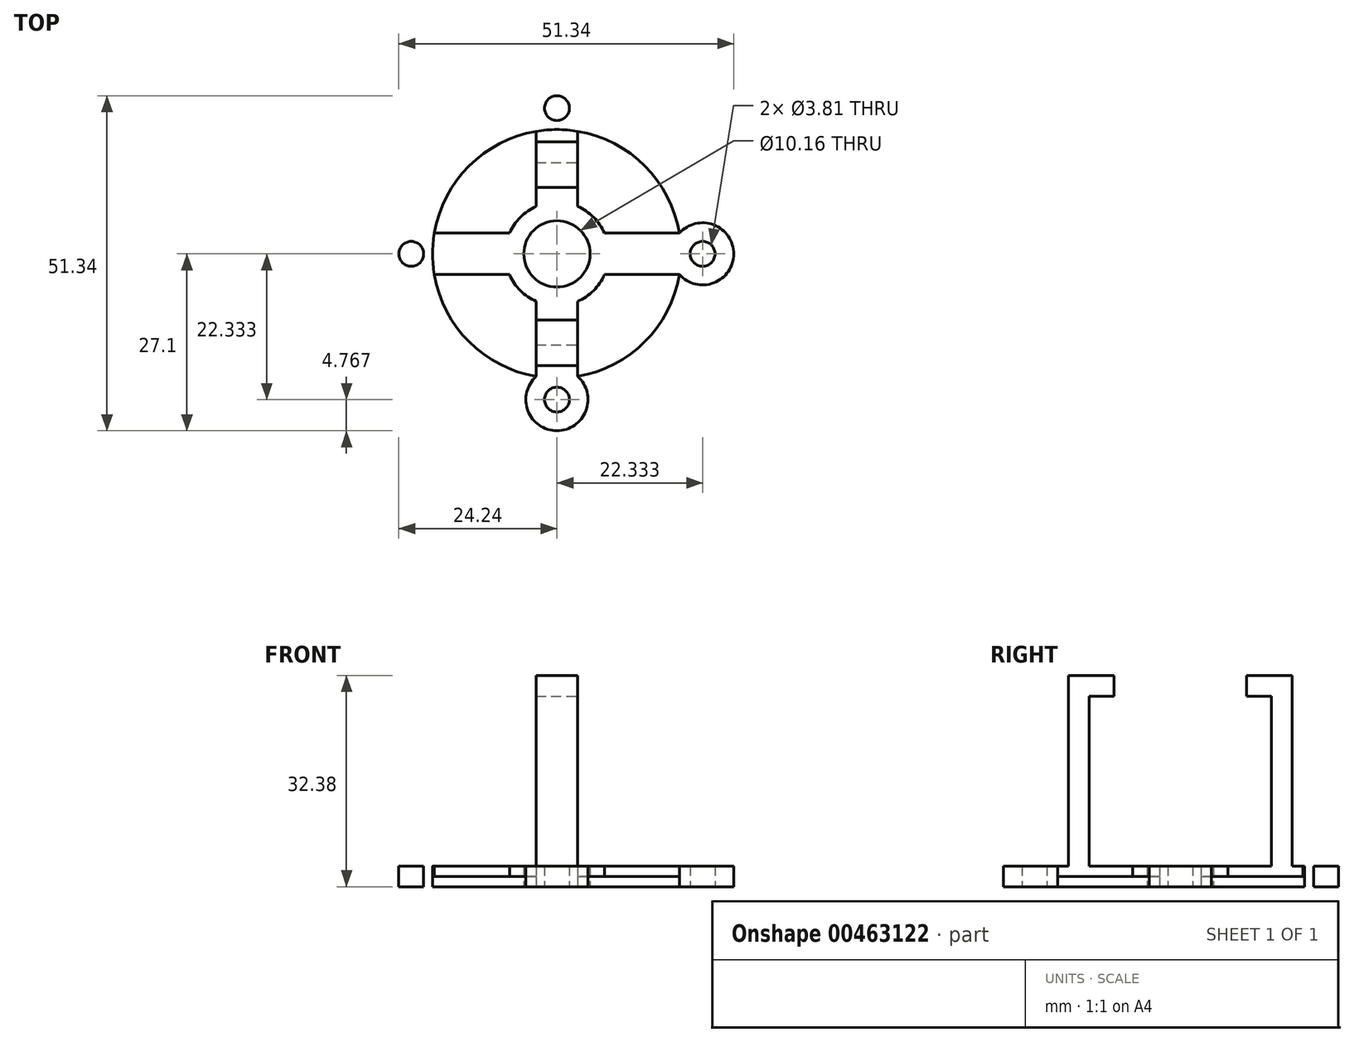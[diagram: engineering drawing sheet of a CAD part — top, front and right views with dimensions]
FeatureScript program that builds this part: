
annotation { "Feature Type Name" : "Feature", "Feature Type Description" : "" }
export const myFeature = defineFeature(function(context is Context, id is Id, definition is map)
    precondition{}
    {
        {
            var Q0;
            Q0=qCreatedBy(makeId("Top.planeOp"),FACE);
            var sketch = newSketch(context, id + "F0", { "sketchPlane" : qUnion([Q0])});
            skCircle(sketch, "E0", {"center": v(0, 0) * mm, "radius": 5.08 * mm});
            skCircle(sketch, "E1", {"center": v(0, 0) * mm, "radius": 19.05 * mm});
            skCircle(sketch, "E2", {"center": v(0, 0) * mm, "radius": 7.94 * mm});
            skLineSegment(sketch, "E3", {"start": v(-3.18, -7.27) * mm, "end": v(-3.18, -18.78) * mm});
            skLineSegment(sketch, "E4", {"start": v(0, 0) * mm, "end": v(3.6, 3.6) * mm});
            skLineSegment(sketch, "E5.MirrorCS", {"start": v(3.18, -7.27) * mm, "end": v(3.18, -18.78) * mm});
            skLineSegment(sketch, "E6.MirrorCS", {"start": v(3.18, 7.27) * mm, "end": v(3.18, 18.78) * mm});
            skLineSegment(sketch, "E7.MirrorCS", {"start": v(-3.18, 7.27) * mm, "end": v(-3.18, 18.78) * mm});
            skLineSegment(sketch, "E8.MirrorCS", {"start": v(-7.27, -3.17) * mm, "end": v(-18.78, -3.17) * mm});
            skLineSegment(sketch, "E9.MirrorCS", {"start": v(-7.27, 3.18) * mm, "end": v(-18.78, 3.18) * mm});
            skLineSegment(sketch, "E10.MirrorCS", {"start": v(7.27, -3.17) * mm, "end": v(18.78, -3.17) * mm});
            skLineSegment(sketch, "E11.MirrorCS", {"start": v(7.27, 3.18) * mm, "end": v(18.78, 3.18) * mm});
            skCircle(sketch, "E12", {"center": v(0, -22.33) * mm, "radius": 4.76 * mm});
            skPoint(sketch, "E12.third.point", {"position": v(3.18, -25.88) * mm});
            skCircle(sketch, "E13.MirrorC", {"center": v(0, 22.33) * mm, "radius": 4.76 * mm});
            skCircle(sketch, "E14.MirrorC", {"center": v(-22.33, 0) * mm, "radius": 4.76 * mm});
            skCircle(sketch, "E15.MirrorC", {"center": v(22.33, 0) * mm, "radius": 4.76 * mm});
            skLineSegment(sketch, "E16.bottom", {"start": v(-3.18, -17.15) * mm, "end": v(3.18, -17.15) * mm});
            skLineSegment(sketch, "E16.top", {"start": v(-3.18, -13.97) * mm, "end": v(3.18, -13.97) * mm});
            skLineSegment(sketch, "E16.left", {"start": v(-3.18, -17.15) * mm, "end": v(-3.18, -13.97) * mm});
            skLineSegment(sketch, "E16.right", {"start": v(3.18, -17.15) * mm, "end": v(3.18, -13.97) * mm});
            skLineSegment(sketch, "E17.MirrorCS", {"start": v(-3.18, 13.97) * mm, "end": v(3.18, 13.97) * mm});
            skLineSegment(sketch, "E18.MirrorCS", {"start": v(-3.18, 17.15) * mm, "end": v(3.18, 17.15) * mm});
            skCircle(sketch, "E19", {"center": v(0, -22.33) * mm, "radius": 1.9 * mm});
            skCircle(sketch, "E20.MirrorC", {"center": v(0, 22.33) * mm, "radius": 1.9 * mm});
            skCircle(sketch, "E21.MirrorC", {"center": v(-22.33, 0) * mm, "radius": 1.9 * mm});
            skCircle(sketch, "E22.MirrorC", {"center": v(22.33, 0) * mm, "radius": 1.9 * mm});
            skSolve(sketch);
        }
        {
            var Q0;
            {var subQ0=sQuery(id+"F0.wireOp",EDGE,"E10.MirrorCS");Q0=makeQuery(id+"F0.imprint","IMPRINT",FACE,{"disambiguationData":[TD([[makeQuery(id+"F0.imprint","IMPRINT",EDGE,{"derivedFrom":subQ0}),1.0]])]});}
            var Q1;
            {var subQ0=sQuery(id+"F0.wireOp",EDGE,"E15.MirrorC");var subQ1=sQuery(id+"F0.wireOp",EDGE,"E1");var subQ2=makeQuery(id+"F0.imprint","INTERSECT",VERTEX,{"derivedFrom":[subQ1,sQuery(id+"F0.wireOp",EDGE,"E10.MirrorCS"),subQ0]});Q1=makeQuery(id+"F0.imprint","IMPRINT",FACE,{"disambiguationData":[TD([[makeQuery(id+"F0.imprint","IMPRINT",EDGE,{"disambiguationData":[TD([[subQ2,-1.0]])],"derivedFrom":subQ1}),1.0]])]});}
            var Q2;
            Q2=makeQuery(id+"F0.imprint","IMPRINT",FACE,{"disambiguationData":[TD([[makeQuery(id+"F0.imprint","IMPRINT",EDGE,{"derivedFrom":sQuery(id+"F0.wireOp",EDGE,"E22.MirrorC")}),-1.0]])]});
            var Q3;
            {var subQ5=sQuery(id+"F0.wireOp",EDGE,"E17.MirrorCS");Q3=makeQuery(id+"F0.imprint","IMPRINT",FACE,{"disambiguationData":[TD([[makeQuery(id+"F0.imprint","IMPRINT",EDGE,{"derivedFrom":subQ5}),-1.0]])]});}
            var Q4;
            Q4=makeQuery(id+"F0.imprint","IMPRINT",FACE,{"disambiguationData":[TD([[makeQuery(id+"F0.imprint","IMPRINT",EDGE,{"derivedFrom":sQuery(id+"F0.wireOp",EDGE,"E0")}),-1.0]])]});
            var Q5;
            {var subQ0=sQuery(id+"F0.wireOp",EDGE,"E8.MirrorCS");Q5=makeQuery(id+"F0.imprint","IMPRINT",FACE,{"disambiguationData":[TD([[makeQuery(id+"F0.imprint","IMPRINT",EDGE,{"derivedFrom":subQ0}),-1.0]])]});}
            var Q6;
            {var subQ4=sQuery(id+"F0.wireOp",EDGE,"E18.MirrorCS");Q6=makeQuery(id+"F0.imprint","IMPRINT",FACE,{"disambiguationData":[TD([[makeQuery(id+"F0.imprint","IMPRINT",EDGE,{"derivedFrom":subQ4}),1.0]])]});}
            var Q7;
            Q7=makeQuery(id+"F0.imprint","IMPRINT",FACE,{"disambiguationData":[TD([[makeQuery(id+"F0.imprint","IMPRINT",EDGE,{"derivedFrom":sQuery(id+"F0.wireOp",EDGE,"E20.MirrorC")}),1.0]])]});
            var Q8;
            {var subQ0=sQuery(id+"F0.wireOp",EDGE,"E13.MirrorC");var subQ1=sQuery(id+"F0.wireOp",EDGE,"E1");var subQ2=makeQuery(id+"F0.imprint","INTERSECT",VERTEX,{"derivedFrom":[subQ1,sQuery(id+"F0.wireOp",EDGE,"E6.MirrorCS"),subQ0]});Q8=makeQuery(id+"F0.imprint","IMPRINT",FACE,{"disambiguationData":[TD([[makeQuery(id+"F0.imprint","IMPRINT",EDGE,{"disambiguationData":[TD([[subQ2,-1.0]])],"derivedFrom":subQ1}),1.0]])]});}
            var Q9;
            {var subQ5=sQuery(id+"F0.wireOp",EDGE,"E16.top");Q9=makeQuery(id+"F0.imprint","IMPRINT",FACE,{"disambiguationData":[TD([[makeQuery(id+"F0.imprint","IMPRINT",EDGE,{"derivedFrom":subQ5}),1.0]])]});}
            var Q10;
            {var subQ4=sQuery(id+"F0.wireOp",EDGE,"E16.bottom");Q10=makeQuery(id+"F0.imprint","IMPRINT",FACE,{"disambiguationData":[TD([[makeQuery(id+"F0.imprint","IMPRINT",EDGE,{"derivedFrom":subQ4}),-1.0]])]});}
            var Q11;
            {var subQ0=sQuery(id+"F0.wireOp",EDGE,"E12");var subQ1=sQuery(id+"F0.wireOp",EDGE,"E1");var subQ2=makeQuery(id+"F0.imprint","INTERSECT",VERTEX,{"derivedFrom":[subQ1,sQuery(id+"F0.wireOp",EDGE,"E3"),subQ0]});Q11=makeQuery(id+"F0.imprint","IMPRINT",FACE,{"disambiguationData":[TD([[makeQuery(id+"F0.imprint","IMPRINT",EDGE,{"disambiguationData":[TD([[subQ2,-1.0]])],"derivedFrom":subQ1}),1.0]])]});}
            var Q12;
            Q12=makeQuery(id+"F0.imprint","IMPRINT",FACE,{"disambiguationData":[TD([[makeQuery(id+"F0.imprint","IMPRINT",EDGE,{"derivedFrom":sQuery(id+"F0.wireOp",EDGE,"E19")}),-1.0]])]});
            var Q13;
            {var subQ0=sQuery(id+"F0.wireOp",EDGE,"E14.MirrorC");var subQ1=sQuery(id+"F0.wireOp",EDGE,"E1");var subQ2=makeQuery(id+"F0.imprint","INTERSECT",VERTEX,{"derivedFrom":[subQ1,sQuery(id+"F0.wireOp",EDGE,"E8.MirrorCS"),subQ0]});Q13=makeQuery(id+"F0.imprint","IMPRINT",FACE,{"disambiguationData":[TD([[makeQuery(id+"F0.imprint","IMPRINT",EDGE,{"disambiguationData":[TD([[subQ2,1.0]])],"derivedFrom":subQ1}),1.0]])]});}
            var Q14;
            Q14=makeQuery(id+"F0.imprint","IMPRINT",FACE,{"disambiguationData":[TD([[makeQuery(id+"F0.imprint","IMPRINT",EDGE,{"derivedFrom":sQuery(id+"F0.wireOp",EDGE,"E21.MirrorC")}),1.0]])]});
            extrude(context, id + "F1", {"entities" : qUnion([Q0, Q1, Q2, Q3, Q4, Q5, Q6, Q7, Q8, Q9, Q10, Q11, Q12, Q13, Q14]), "depth" : 3.17 * mm});
        }
        {
            var Q0;
            {var subQ5=sQuery(id+"F0.wireOp",EDGE,"E11.MirrorCS");Q0=makeQuery(id+"F0.imprint","IMPRINT",FACE,{"disambiguationData":[TD([[makeQuery(id+"F0.imprint","IMPRINT",EDGE,{"derivedFrom":subQ5}),1.0]])]});}
            var Q1;
            {var subQ6=sQuery(id+"F0.wireOp",EDGE,"E10.MirrorCS");Q1=makeQuery(id+"F0.imprint","IMPRINT",FACE,{"disambiguationData":[TD([[makeQuery(id+"F0.imprint","IMPRINT",EDGE,{"derivedFrom":subQ6}),-1.0]])]});}
            var Q2;
            {var subQ5=sQuery(id+"F0.wireOp",EDGE,"E9.MirrorCS");Q2=makeQuery(id+"F0.imprint","IMPRINT",FACE,{"disambiguationData":[TD([[makeQuery(id+"F0.imprint","IMPRINT",EDGE,{"derivedFrom":subQ5}),-1.0]])]});}
            var Q3;
            {var subQ6=sQuery(id+"F0.wireOp",EDGE,"E8.MirrorCS");Q3=makeQuery(id+"F0.imprint","IMPRINT",FACE,{"disambiguationData":[TD([[makeQuery(id+"F0.imprint","IMPRINT",EDGE,{"derivedFrom":subQ6}),1.0]])]});}
            extrude(context, id + "F2", {"entities" : qUnion([Q0, Q1, Q2, Q3]), "operationType" : NewBodyOperationType.ADD, "depth" : 1.56 * mm});
        }
        {
            var Q0;
            Q0=makeQuery(id+"F0.imprint","IMPRINT",FACE,{"disambiguationData":[TD([[makeQuery(id+"F0.imprint","IMPRINT",EDGE,{"derivedFrom":sQuery(id+"F0.wireOp",EDGE,"E16.bottom")}),1.0]])]});
            var Q1;
            {var subQ0=sQuery(id+"F0.wireOp",EDGE,"E17.MirrorCS");Q1=makeQuery(id+"F0.imprint","IMPRINT",FACE,{"disambiguationData":[TD([[makeQuery(id+"F0.imprint","IMPRINT",EDGE,{"derivedFrom":subQ0}),1.0]])]});}
            extrude(context, id + "F3", {"entities" : qUnion([Q0, Q1]), "operationType" : NewBodyOperationType.ADD, "depth" : 32.38 * mm});
        }
        {
            var Q0;
            Q0=makeQuery(id+"F3.opExtrude","SWEPT_FACE",FACE,{"disambiguationData":[OSD([sQuery(id+"F0.wireOp",EDGE,"E17.MirrorCS")])]});
            var sketch = newSketch(context, id + "F4", { "sketchPlane" : qUnion([Q0])});
            skLineSegment(sketch, "E23", {"start": v(-3.18, 29.21) * mm, "end": v(3.18, 29.21) * mm});
            skSolve(sketch);
        }
        {
            var Q0;
            Q0=makeQuery(id+"F3.opExtrude","SWEPT_FACE",FACE,{"disambiguationData":[OSD([sQuery(id+"F0.wireOp",EDGE,"E16.top")])]});
            var sketch = newSketch(context, id + "F5", { "sketchPlane" : qUnion([Q0])});
            skLineSegment(sketch, "E24", {"start": v(-3.18, 29.21) * mm, "end": v(3.18, 29.21) * mm});
            skSolve(sketch);
        }
        {
            var Q0;
            {var subQ0=sQuery(id+"F5.wireOp",EDGE,"E24");Q0=makeQuery(id+"F5.imprint","IMPRINT",FACE,{"disambiguationData":[TD([[makeQuery(id+"F5.imprint","IMPRINT",EDGE,{"derivedFrom":subQ0}),1.0]])]});}
            extrude(context, id + "F6", {"entities" : qUnion([Q0]), "operationType" : NewBodyOperationType.ADD, "depth" : 3.8 * mm});
        }
        {
            var Q0;
            {var subQ0=sQuery(id+"F4.wireOp",EDGE,"E23");Q0=makeQuery(id+"F4.imprint","IMPRINT",FACE,{"disambiguationData":[TD([[makeQuery(id+"F4.imprint","IMPRINT",EDGE,{"derivedFrom":subQ0}),1.0]])]});}
            extrude(context, id + "F7", {"entities" : qUnion([Q0]), "operationType" : NewBodyOperationType.ADD, "depth" : 3.8 * mm});
        }
    });
